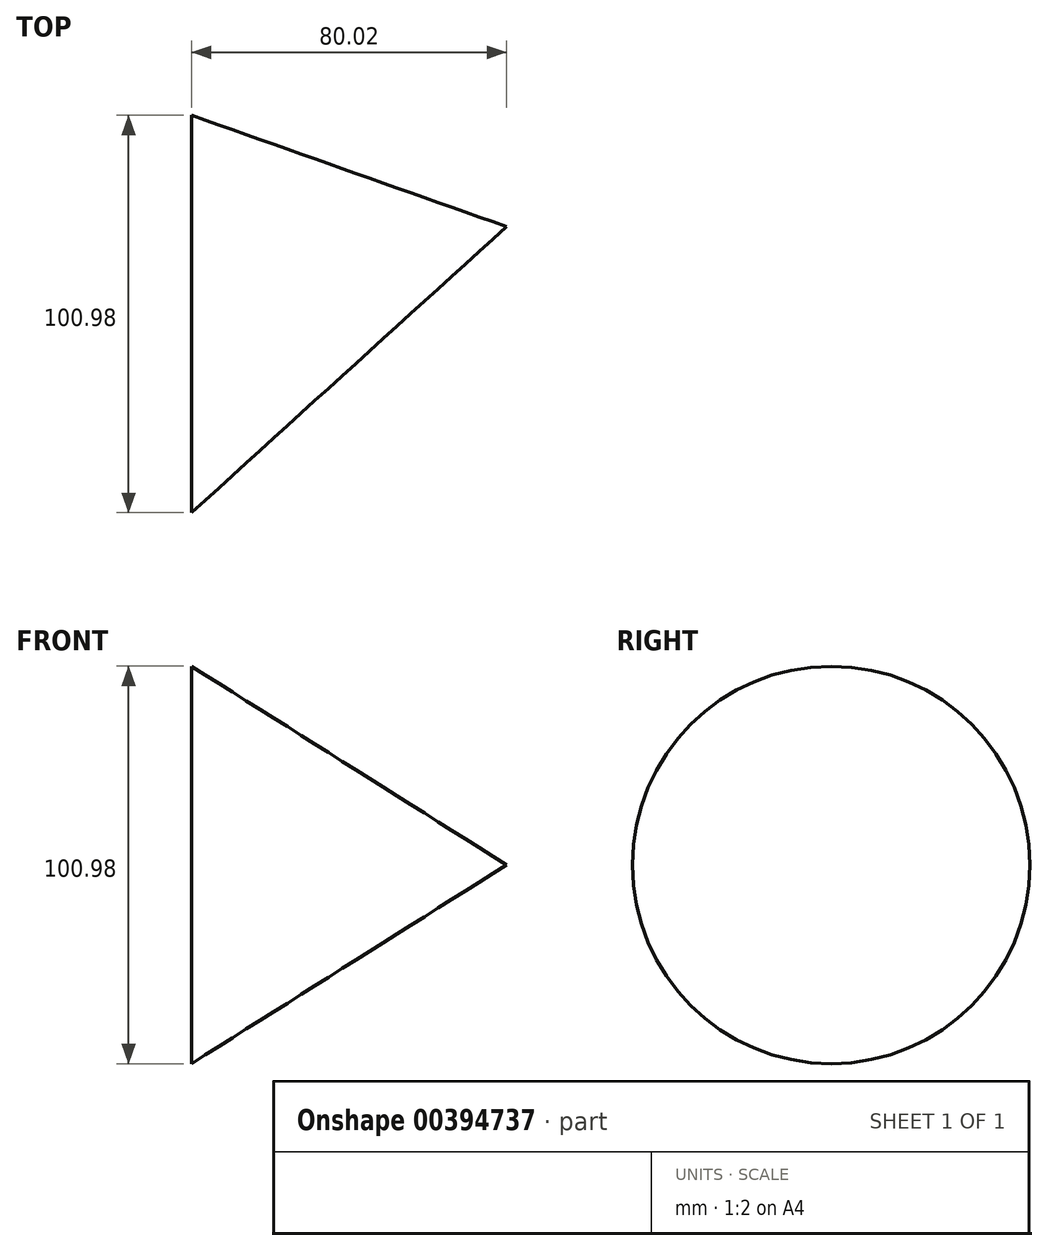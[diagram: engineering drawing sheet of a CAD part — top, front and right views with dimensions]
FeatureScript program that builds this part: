
annotation { "Feature Type Name" : "Feature", "Feature Type Description" : "" }
export const myFeature = defineFeature(function(context is Context, id is Id, definition is map)
    precondition{}
    {
        {
            var Q0;
            Q0=qCreatedBy(makeId("Top.planeOp"),FACE);
            var sketch = newSketch(context, id + "F0", { "sketchPlane" : qUnion([Q0])});
            skLineSegment(sketch, "E0.bottom", {"start": v(58.2, 61.47) * mm, "end": v(-58.2, 61.47) * mm});
            skLineSegment(sketch, "E0.top", {"start": v(58.2, -61.47) * mm, "end": v(-58.2, -61.47) * mm});
            skLineSegment(sketch, "E0.left", {"start": v(58.2, 61.47) * mm, "end": v(58.2, -61.47) * mm});
            skLineSegment(sketch, "E0.right", {"start": v(-58.2, 61.47) * mm, "end": v(-58.2, -61.47) * mm});
            skPoint(sketch, "E0.middle", {"position": v(0, 0) * mm});
            skCircle(sketch, "E1", {"center": v(0, 0) * mm, "radius": 40.5 * mm});
            skSolve(sketch);
        }
        {
            var Q0;
            Q0=makeQuery(id+"F0.imprint","IMPRINT",FACE,{"disambiguationData":[TD([[makeQuery(id+"F0.imprint","IMPRINT",EDGE,{"derivedFrom":sQuery(id+"F0.wireOp",EDGE,"E1")}),1.0]])]});
            extrude(context, id + "F1", {"entities" : qUnion([Q0]), "depth" : 554.8 * mm});
        }
        {
            var Q0;
            Q0=makeQuery(id+"F1.opExtrude","SWEPT_BODY",BODY,{"disambiguationData":[OSD([sQuery(id+"F0.wireOp",EDGE,"E1")])]});
            deleteBodies(context, id + "F2", {"entities" : qUnion([Q0])});
        }
        {
            var Q0;
            Q0=qCreatedBy(makeId("Right.planeOp"),FACE);
            var sketch = newSketch(context, id + "F3", { "sketchPlane" : qUnion([Q0])});
            skCircle(sketch, "E2", {"center": v(0, 0) * mm, "radius": 50.49 * mm});
            skSolve(sketch);
        }
        {
            var Q0;
            Q0=qCreatedBy(makeId("Top.planeOp"),FACE);
            var sketch = newSketch(context, id + "F4", { "sketchPlane" : qUnion([Q0])});
            skLineSegment(sketch, "E3.bottom", {"start": v(80.02, 22.19) * mm, "end": v(48.01, 22.19) * mm});
            skLineSegment(sketch, "E3.top", {"start": v(80.02, -22.19) * mm, "end": v(48.01, -22.19) * mm});
            skLineSegment(sketch, "E3.left", {"start": v(80.02, 22.19) * mm, "end": v(80.02, -22.19) * mm});
            skLineSegment(sketch, "E3.right", {"start": v(48.01, 22.19) * mm, "end": v(48.01, -22.19) * mm});
            skPoint(sketch, "E3.middle", {"position": v(64.02, 0) * mm});
            skSolve(sketch);
        }
        {
            var Q0;
            Q0=sQuery(id+"F4.wireOp",VERTEX,"E3.left.start");
            var Q1;
            Q1 = qSketchRegion(id + "F3", true);
            loft(context, id + "F5", {"sheetProfilesArray" : [{ "sheetProfileEntities" : qUnion([Q0]) }, { "sheetProfileEntities" : qUnion([Q1]) }]});
        }
    });
